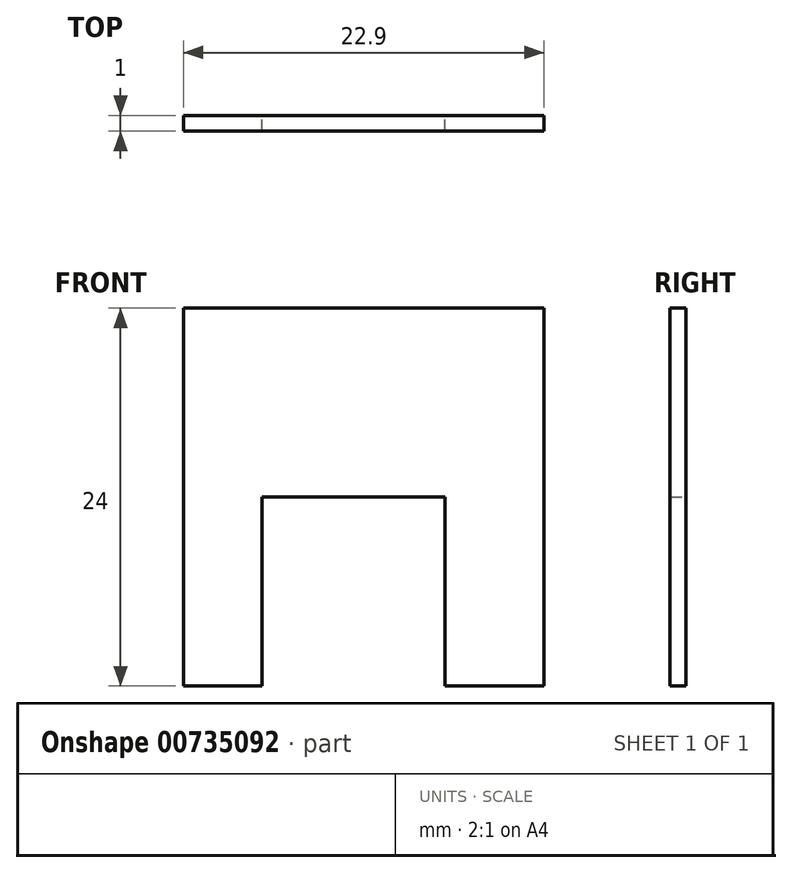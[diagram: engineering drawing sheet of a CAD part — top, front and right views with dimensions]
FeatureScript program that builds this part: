
annotation { "Feature Type Name" : "Feature", "Feature Type Description" : "" }
export const myFeature = defineFeature(function(context is Context, id is Id, definition is map)
    precondition{}
    {
        {
            var Q0;
            Q0=qCreatedBy(makeId("Front.planeOp"),FACE);
            var sketch = newSketch(context, id + "F0", { "sketchPlane" : qUnion([Q0])});
            skLineSegment(sketch, "E0", {"start": v(0, 0) * mm, "end": v(-5, 0) * mm});
            skLineSegment(sketch, "E1", {"start": v(-5, 0) * mm, "end": v(-5, 24) * mm});
            skLineSegment(sketch, "E2", {"start": v(-5, 24) * mm, "end": v(17.9, 24) * mm});
            skLineSegment(sketch, "E3", {"start": v(17.9, 24) * mm, "end": v(17.9, 0) * mm});
            skLineSegment(sketch, "E4", {"start": v(17.9, 0) * mm, "end": v(11.6, 0) * mm});
            skLineSegment(sketch, "E5", {"start": v(11.6, 0) * mm, "end": v(11.6, 12) * mm});
            skLineSegment(sketch, "E6", {"start": v(11.6, 12) * mm, "end": v(0, 12) * mm});
            skLineSegment(sketch, "E7", {"start": v(0, 12) * mm, "end": v(0, 0) * mm});
            skSolve(sketch);
        }
        {
            var Q0;
            Q0=makeQuery(id+"F0.imprint","IMPRINT",FACE,{"disambiguationData":[TD([[makeQuery(id+"F0.imprint","IMPRINT",EDGE,{"derivedFrom":sQuery(id+"F0.wireOp",EDGE,"E0")}),-1.0]])]});
            extrude(context, id + "F1", {"entities" : qUnion([Q0]), "depth" : 1 * mm, "offsetDistance" : 25 * mm});
        }
    });
